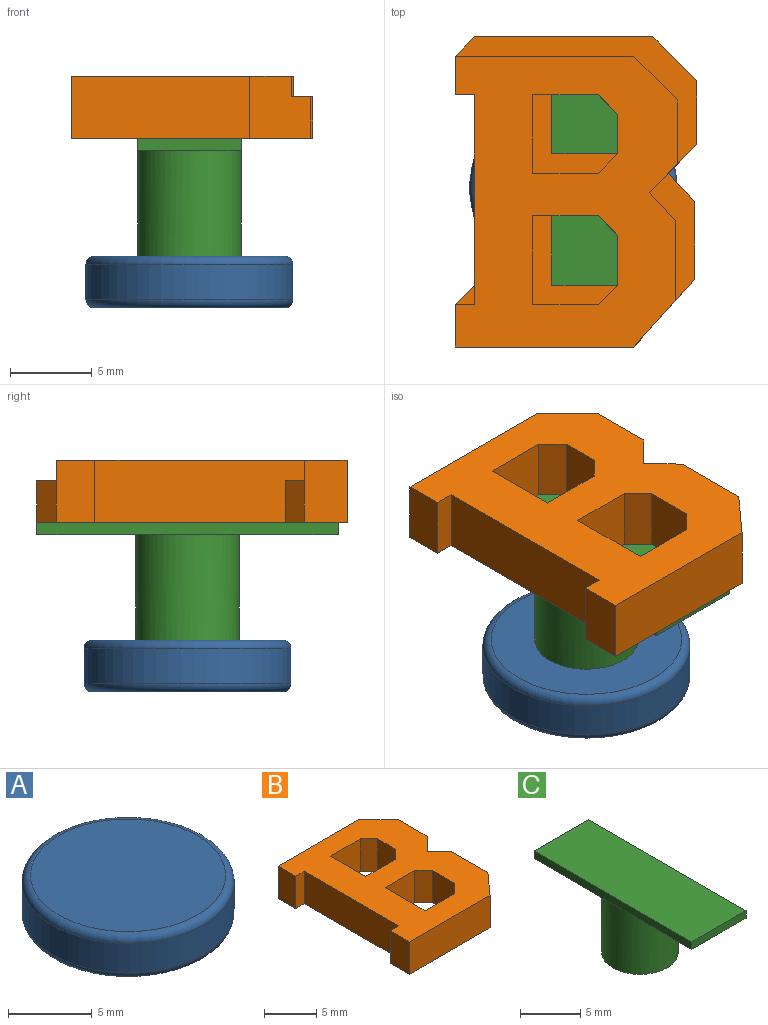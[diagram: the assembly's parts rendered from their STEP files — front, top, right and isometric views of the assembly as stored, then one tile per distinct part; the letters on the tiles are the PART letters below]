
ASSEMBLY  parts=3 mates=3
PART A: 5 faces, bbox 13.7x13.7x3.2 mm
  f0: cylinder r=6.35mm len=12.7mm, axis (0,0,1), area 86.1mm2, adj f3,f4
  f1: plane 11.68x11.68mm, normal (0,0,-1), area 107.2mm2, adj f4
  f2: plane 11.68x11.68mm, normal (0,0,1), area 107.2mm2, adj f3
  f3: torus R=5.84mm, axis (0,0,1), area 30.9mm2, adj f0,f2
  f4: torus R=5.84mm, axis (0,0,1), area 30.9mm2, adj f0,f1
PART B: 43 faces, bbox 14.8x19x3.8 mm
  f0: plane 17.85x13.65mm, normal (0,0,1), area 166.3mm2, adj f3,f6,f7,f8,f9,f10,f11,f13
  f1: plane 4.05x2.54mm, normal (0,1,0), area 10.3mm2, adj f2,f7,f25,f41
  f2: plane 3.62x2.54mm, normal (1,0,0), area 9.2mm2, adj f1,f24,f25,f41
  f3: plane 3.81x2.93mm, normal (0.71,-0.71,0), area 9.4mm2, adj f0,f17,f18,f25,f34,f35,f36,f38
  f4: plane 4.05x2.54mm, normal (0,1,0), area 10.3mm2, adj f5,f10,f25,f31
  f5: plane 4.25x2.54mm, normal (1,0,0), area 10.8mm2, adj f4,f8,f25,f31
  f6: plane 3.81x1.18mm, normal (-0.71,-0.71,0), area 6.4mm2, adj f0,f7,f24,f25
  f7: plane 3.81x2.44mm, normal (-1,0,0), area 9.3mm2, adj f0,f1,f6,f25,f40
  f8: plane 4.05x3.81mm, normal (0,-1,0), area 12.4mm2, adj f0,f5,f9,f25,f30,f31
  f9: plane 3.81x1.18mm, normal (-0.71,-0.71,0), area 6.4mm2, adj f0,f8,f10,f25
  f10: plane 3.81x3.07mm, normal (-1,0,0), area 11.7mm2, adj f0,f4,f9,f25,f29
  f11: plane 12.85x3.81mm, normal (-1,0,0), area 46mm2, adj f0,f12,f23,f25,f26,f27
  f12: plane 2.54x1.18mm, normal (-0.71,0.71,0), area 4.2mm2, adj f11,f13,f25,f27
  f13: plane 3.81x2.62mm, normal (-1,0,0), area 10mm2, adj f0,f12,f14,f25,f26
  f14: plane 10.95x3.81mm, normal (0,-1,0), area 41.7mm2, adj f0,f13,f15,f25
  f15: plane 4.16x3.81mm, normal (0.74,-0.67,0), area 19.1mm2, adj f0,f14,f16,f25,f37,f38
  f16: plane 4.76x2.54mm, normal (1,0,0), area 12.1mm2, adj f15,f17,f25,f38
  f17: plane 2.54x1.75mm, normal (0.73,0.68,0), area 6mm2, adj f3,f16,f25,f38
  f18: plane 3.92x2.54mm, normal (1,0,0), area 9.9mm2, adj f3,f19,f25,f35
  f19: plane 2.69x2.69mm, normal (0.71,0.71,0), area 9.7mm2, adj f18,f20,f25,f35
  f20: plane 10.95x2.54mm, normal (0,1,0), area 27.8mm2, adj f19,f21,f25,f35
  f21: plane 2.54x1.18mm, normal (-0.71,0.71,0), area 4.2mm2, adj f20,f22,f25,f35
  f22: plane 3.81x2.38mm, normal (-1,0,0), area 9.1mm2, adj f0,f21,f23,f25,f32
  f23: plane 3.81x1.18mm, normal (0,-1,0), area 4.5mm2, adj f0,f11,f22,f25
  f24: plane 4.05x3.81mm, normal (0,-1,0), area 12.4mm2, adj f0,f2,f6,f25,f41,f42
  f25: plane 19.03x14.83mm, normal (0,0,-1), area 220.7mm2, adj f1,f2,f3,f4,f5,f6,f7,f8
  f26: plane 1.27x1.18mm, normal (0,1,0), area 1.5mm2, adj f0,f11,f13,f27
  f27: plane 1.18x1.18mm, normal (0,0,1), area 0.7mm2, adj f11,f12,f26
  f28: plane 4.05x1.27mm, normal (0,1,0), area 5.1mm2, adj f0,f29,f30,f31
  f29: plane 1.27x1.18mm, normal (-0.71,0.71,0), area 2.1mm2, adj f0,f10,f28,f31
  f30: plane 5.43x1.27mm, normal (1,0,0), area 6.9mm2, adj f0,f8,f28,f31
  f31: plane 5.43x5.23mm, normal (0,0,1), area 10.5mm2, adj f4,f5,f8,f28,f29,f30
  f32: plane 10.95x1.27mm, normal (0,1,0), area 13.9mm2, adj f0,f22,f33,f35
  f33: plane 2.69x2.69mm, normal (0.71,0.71,0), area 4.8mm2, adj f0,f32,f34,f35
  f34: plane 3.92x1.27mm, normal (1,0,0), area 5mm2, adj f0,f3,f33,f35
  f35: plane 14.83x7.79mm, normal (0,0,1), area 23.9mm2, adj f3,f18,f19,f20,f21,f32,f33,f34
  f36: plane 1.75x1.62mm, normal (0.73,0.68,0), area 3mm2, adj f0,f3,f37,f38
  f37: plane 4.89x1.27mm, normal (1,0,0), area 6.2mm2, adj f0,f15,f36,f38
  f38: plane 7.82x2.79mm, normal (0,0,1), area 9.7mm2, adj f3,f15,f16,f17,f36,f37
  f39: plane 4.05x1.27mm, normal (0,1,0), area 5.1mm2, adj f0,f40,f41,f42
  f40: plane 1.27x1.18mm, normal (-0.71,0.71,0), area 2.1mm2, adj f0,f7,f39,f41
  f41: plane 5.23x4.8mm, normal (0,0,1), area 9.7mm2, adj f1,f2,f24,f39,f40,f42
  f42: plane 4.8x1.27mm, normal (1,0,0), area 6.1mm2, adj f0,f24,f39,f41
PART C: 9 faces, bbox 6.4x18.5x7.2 mm
  f0: cylinder r=3.17mm len=6.48mm, axis (0,0,-1), area 129.2mm2, adj f1,f2,f8
  f1: plane 6.35x6.35mm, normal (0,0,-1), area 31.7mm2, adj f0
  f2: plane 9.24x6.35mm, normal (0,0,-1), area 42.8mm2, adj f0,f4,f5,f6
  f3: plane 6.35x0.76mm, normal (0,-1,0), area 4.8mm2, adj f4,f6,f7,f8
  f4: plane 18.48x0.76mm, normal (1,0,0), area 14.1mm2, adj f2,f3,f5,f7,f8
  f5: plane 6.35x0.76mm, normal (0,1,0), area 4.8mm2, adj f2,f4,f6,f7
  f6: plane 18.48x0.76mm, normal (-1,0,0), area 14.1mm2, adj f2,f3,f5,f7,f8
  f7: plane 18.48x6.35mm, normal (0,0,1), area 117.3mm2, adj f3,f4,f5,f6
  f8: plane 9.24x6.35mm, normal (0,0,-1), area 42.8mm2, adj f0,f3,f4,f6
PLACE A t=(1.96,2.57,-1.9)mm fixed
PLACE B t=(8.07,-2.33,9.15)mm
PLACE C t=(1.96,2.57,-1.9)mm
MATE fastened C.f0 <-> A.f0  axis (0,0,-1) through (1.96,2.57,-1.9)mm
MATE planar C.f0 <-> B.f25  axis (0,0,1) through (1.96,2.57,5.34)mm
MATE planar B.f20 <-> C.f5  axis (0,1,0) through (1.37,11.81,6.61)mm
